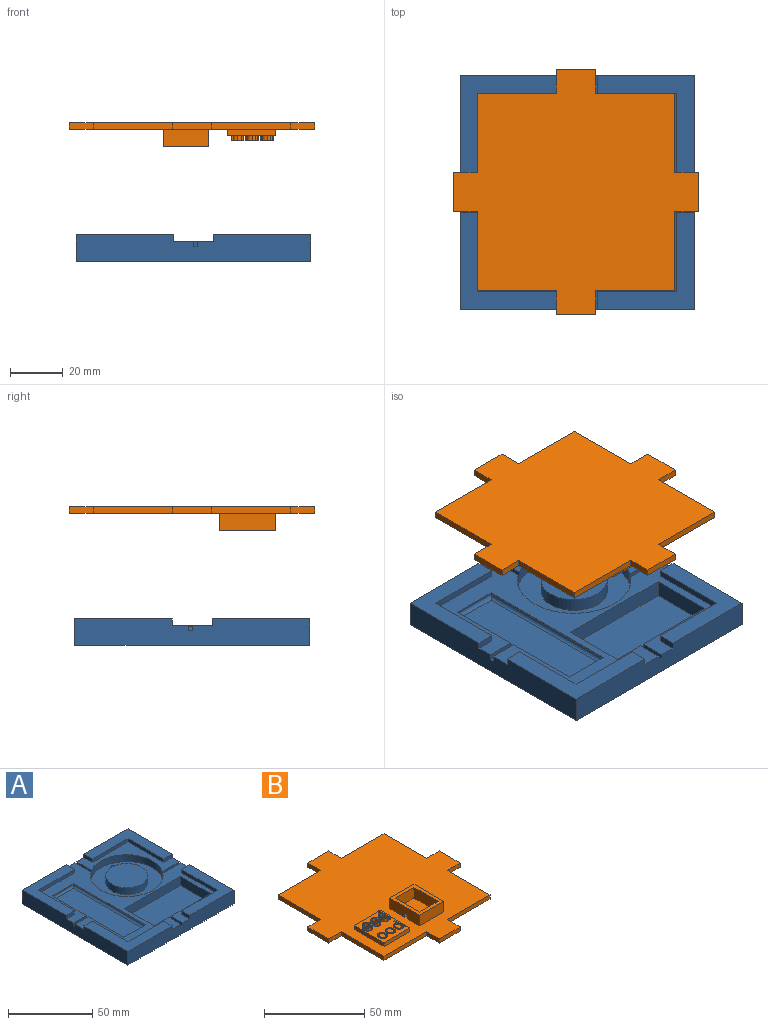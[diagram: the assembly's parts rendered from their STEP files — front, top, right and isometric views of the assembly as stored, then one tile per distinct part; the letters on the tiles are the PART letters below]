
ASSEMBLY  parts=2 mates=1
PART A: 59 faces, bbox 88.9x88.9x10 mm
  f0: cylinder r=21.5mm len=43mm, axis (0,0,1), area 662.5mm2, adj f1,f2,f40,f50,f51,f52,f53,f54
  f1: plane 42.95x42.95mm, normal (0,0,1), area 414.7mm2, adj f0,f3,f5,f14,f27,f28,f29,f50
  f2: plane 88.9x88.9mm, normal (0,0,1), area 1847.3mm2, adj f0,f3,f4,f5,f6,f7,f15,f16
  f3: plane 88.9x10mm, normal (1,0,0), area 844mm2, adj f1,f2,f4,f5,f9,f12,f13,f26
  f4: plane 88.9x10mm, normal (0,-1,0), area 848.5mm2, adj f2,f3,f6,f11,f12,f13,f22,f23
  f5: plane 88.9x10mm, normal (0,1,0), area 848.5mm2, adj f1,f2,f3,f6,f9,f10,f13,f14
  f6: plane 88.9x10mm, normal (-1,0,0), area 848.5mm2, adj f2,f4,f5,f10,f11,f13,f18,f19
  f7: plane 30x0.55mm, normal (1,0,0), area 16.5mm2, adj f2,f8,f33,f55
  f8: cylinder r=1.45mm len=30mm, axis (0,-1,0), area 67.1mm2, adj f7,f34,f37,f55
  f9: plane 36.95x36.95mm, normal (0,0,1), area 465.3mm2, adj f3,f5,f14,f27,f28,f29
  f10: plane 36.95x36.95mm, normal (0,0,1), area 465.3mm2, adj f5,f6,f15,f16,f17,f18
  f11: plane 36.95x36.95mm, normal (0,0,1), area 465.3mm2, adj f4,f6,f19,f20,f21,f22
  f12: plane 36.95x36.95mm, normal (0,0,1), area 465.3mm2, adj f3,f4,f23,f24,f25,f26
  f13: plane 88.9x88.9mm, normal (0,0,-1), area 7903.2mm2, adj f3,f4,f5,f6
  f14: plane 6.95x2.5mm, normal (-1,0,0), area 17.4mm2, adj f1,f5,f9,f29
  f15: plane 6.95x2.5mm, normal (1,0,0), area 17.4mm2, adj f2,f5,f10,f16
  f16: plane 30x2.5mm, normal (0,-1,0), area 75mm2, adj f2,f10,f15,f17
  f17: plane 30x2.5mm, normal (1,0,0), area 75mm2, adj f2,f10,f16,f18
  f18: plane 6.95x2.5mm, normal (0,-1,0), area 17.4mm2, adj f2,f6,f10,f17
  f19: plane 6.95x2.5mm, normal (0,1,0), area 17.4mm2, adj f2,f6,f11,f20
  f20: plane 30x2.5mm, normal (1,0,0), area 75mm2, adj f2,f11,f19,f21
  f21: plane 30x2.5mm, normal (0,1,0), area 75mm2, adj f2,f11,f20,f22
  f22: plane 6.95x2.5mm, normal (1,0,0), area 17.4mm2, adj f2,f4,f11,f21
  f23: plane 6.95x2.5mm, normal (-1,0,0), area 17.4mm2, adj f2,f4,f12,f24
  f24: plane 30x2.5mm, normal (0,1,0), area 75mm2, adj f2,f12,f23,f25
  f25: plane 30x2.5mm, normal (-1,0,0), area 75mm2, adj f2,f12,f24,f26
  f26: plane 6.95x2.5mm, normal (0,1,0), area 17.4mm2, adj f2,f3,f12,f25
  f27: plane 6.95x2.5mm, normal (0,-1,0), area 17.4mm2, adj f1,f3,f9,f28
  f28: plane 30x2.5mm, normal (-1,0,0), area 75mm2, adj f1,f9,f27,f29
  f29: plane 30x2.5mm, normal (0,-1,0), area 75mm2, adj f1,f9,f14,f28
  f30: plane 60x0.55mm, normal (-1,0,0), area 33.1mm2, adj f2,f31,f33,f35
  f31: plane 18x0.55mm, normal (0,-1,0), area 9.9mm2, adj f2,f30,f32,f36
  f32: plane 28.5x0.55mm, normal (1,0,0), area 15.7mm2, adj f2,f31,f38,f56
  f33: plane 18x0.55mm, normal (0,1,0), area 9.9mm2, adj f2,f7,f30,f37
  f34: plane 57.1x27.5mm, normal (0,0,1), area 881mm2, adj f6,f8,f35,f36,f37,f38,f55,f56
  f35: cylinder r=1.45mm len=60mm, axis (0,1,0), area 134.1mm2, adj f30,f34,f36,f37
  f36: cylinder r=1.45mm len=18mm, axis (-1,0,0), area 38.6mm2, adj f31,f34,f35,f38
  f37: cylinder r=1.45mm len=18mm, axis (1,0,0), area 38.6mm2, adj f8,f33,f34,f35
  f38: cylinder r=1.45mm len=28.5mm, axis (0,-1,0), area 63.6mm2, adj f32,f34,f36,f56
  f39: cylinder r=12.5mm len=25mm, axis (0,0,1), area 392.7mm2, adj f40,f41
  f40: plane 53.45x43mm, normal (0,0,1), area 975.5mm2, adj f0,f3,f39,f50,f51,f58
  f41: plane 25x25mm, normal (0,0,1), area 490.9mm2, adj f39
  f42: plane 47x6.5mm, normal (0,-1,0), area 305.5mm2, adj f2,f43,f45,f46
  f43: plane 25x6.5mm, normal (1,0,0), area 162.5mm2, adj f2,f42,f44,f46
  f44: plane 47x6.5mm, normal (0,1,0), area 302.5mm2, adj f2,f43,f45,f46,f47,f48,f49
  f45: plane 25x6.5mm, normal (-1,0,0), area 162.5mm2, adj f2,f42,f44,f46
  f46: plane 47x25mm, normal (0,0,1), area 1175mm2, adj f42,f43,f44,f45
  f47: plane 9.95x1.5mm, normal (0,0,1), area 14.9mm2, adj f4,f44,f48,f49
  f48: plane 9.95x2mm, normal (1,0,0), area 19.9mm2, adj f2,f4,f44,f47
  f49: plane 9.95x2mm, normal (-1,0,0), area 19.9mm2, adj f2,f4,f44,f47
  f50: plane 14.11x5mm, normal (0,-1,0), area 70.6mm2, adj f0,f1,f3,f40
  f51: plane 15.22x5mm, normal (0,1,0), area 76.1mm2, adj f0,f2,f3,f40
  f52: plane 13.46x1.5mm, normal (0,0,1), area 19.4mm2, adj f0,f5,f53,f54
  f53: plane 12.48x2mm, normal (-1,0,0), area 25mm2, adj f0,f1,f5,f52
  f54: plane 13.46x2mm, normal (1,0,0), area 26.9mm2, adj f0,f2,f5,f52
  f55: plane 12.4x2mm, normal (0,1,0), area 22.4mm2, adj f2,f6,f7,f8,f34
  f56: plane 12.4x2mm, normal (0,-1,0), area 22.4mm2, adj f2,f6,f32,f34,f38
  f57: plane 0.16x0.16mm, normal (0,0,1), area 0mm2, adj f58
  f58: torus R=0.08mm, axis (0,0,1), area 15.3mm2, adj f40,f57
PART B: 167 faces, bbox 92.8x92.8x9 mm
  f0: plane 21x18.16mm, normal (0,0,1), area 257.9mm2, adj f35,f36,f37,f38,f39,f40,f41,f42
  f1: plane 92.8x92.8mm, normal (0,0,1), area 5614.5mm2, adj f2,f3,f4,f5,f6,f7,f8,f9
  f2: plane 9x2.5mm, normal (-1,0,0), area 22.5mm2, adj f1,f3,f21,f22
  f3: plane 30x2.5mm, normal (0,1,0), area 75mm2, adj f1,f2,f4,f22
  f4: plane 30x2.5mm, normal (-1,0,0), area 75mm2, adj f1,f3,f5,f22
  f5: plane 9x2.5mm, normal (0,1,0), area 22.5mm2, adj f1,f4,f6,f22
  f6: plane 14.8x2.5mm, normal (-1,0,0), area 37mm2, adj f1,f5,f7,f22
  f7: plane 9x2.5mm, normal (0,-1,0), area 22.5mm2, adj f1,f6,f8,f22
  f8: plane 30x2.5mm, normal (-1,0,0), area 75mm2, adj f1,f7,f9,f22
  f9: plane 30x2.5mm, normal (0,-1,0), area 75mm2, adj f1,f8,f10,f22
  f10: plane 9x2.5mm, normal (-1,0,0), area 22.5mm2, adj f1,f9,f11,f22
  f11: plane 14.8x2.5mm, normal (0,-1,0), area 37mm2, adj f1,f10,f12,f22
  f12: plane 9x2.5mm, normal (1,0,0), area 22.5mm2, adj f1,f11,f13,f22
  f13: plane 30x2.5mm, normal (0,-1,0), area 75mm2, adj f1,f12,f14,f22
  f14: plane 30x2.5mm, normal (1,0,0), area 75mm2, adj f1,f13,f15,f22
  f15: plane 9x2.5mm, normal (0,-1,0), area 22.5mm2, adj f1,f14,f16,f22
  f16: plane 14.8x2.5mm, normal (1,0,0), area 37mm2, adj f1,f15,f17,f22
  f17: plane 9x2.5mm, normal (0,1,0), area 22.5mm2, adj f1,f16,f18,f22
  f18: plane 30x2.5mm, normal (1,0,0), area 75mm2, adj f1,f17,f19,f22
  f19: plane 30x2.5mm, normal (0,1,0), area 75mm2, adj f1,f18,f20,f22
  f20: plane 9x2.5mm, normal (1,0,0), area 22.5mm2, adj f1,f19,f21,f22
  f21: plane 14.8x2.5mm, normal (0,1,0), area 37mm2, adj f1,f2,f20,f22
  f22: plane 92.8x92.8mm, normal (0,0,-1), area 6127.8mm2, adj f2,f3,f4,f5,f6,f7,f8,f9
  f23: plane 17x6.48mm, normal (0,1,0), area 110.2mm2, adj f1,f24,f30,f31
  f24: plane 21x6.48mm, normal (-1,0,0), area 132.1mm2, adj f1,f23,f25,f31,f32,f33,f34
  f25: plane 17x6.48mm, normal (0,-1,0), area 110.2mm2, adj f1,f24,f30,f31
  f26: plane 13x6.48mm, normal (0,-1,0), area 84.2mm2, adj f1,f27,f29,f31
  f27: plane 17x6.48mm, normal (-1,0,0), area 110.2mm2, adj f1,f26,f28,f31
  f28: plane 13x6.48mm, normal (0,1,0), area 84.2mm2, adj f1,f27,f29,f31
  f29: plane 17x6.48mm, normal (1,0,0), area 106.2mm2, adj f1,f26,f28,f31,f32,f33,f34
  f30: plane 21x6.48mm, normal (1,0,0), area 136.1mm2, adj f1,f23,f25,f31
  f31: plane 21x17mm, normal (0,0,1), area 136mm2, adj f23,f24,f25,f26,f27,f28,f29,f30
  f32: plane 2x2mm, normal (0,-1,0), area 4mm2, adj f1,f24,f29,f34
  f33: plane 2x2mm, normal (0,1,0), area 4mm2, adj f1,f24,f29,f34
  f34: plane 2x2mm, normal (0,0,-1), area 4mm2, adj f24,f29,f32,f33
  f35: plane 18.16x2.3mm, normal (0,1,0), area 41.8mm2, adj f0,f1,f36,f38
  f36: plane 21x2.3mm, normal (-1,0,0), area 48.3mm2, adj f0,f1,f35,f37
  f37: plane 18.16x2.3mm, normal (0,-1,0), area 41.8mm2, adj f0,f1,f36,f38
  f38: plane 21x2.3mm, normal (1,0,0), area 48.3mm2, adj f0,f1,f35,f37
  f39: extruded ~1.93x1.9mm, area 3.9mm2, adj f0,f40,f47,f72
  f40: extruded ~1.91x1.9mm, area 3.9mm2, adj f0,f39,f41,f72
  f41: extruded ~1.9x1.68mm, area 3.6mm2, adj f0,f40,f42,f72
  f42: extruded ~1.9x1.72mm, area 3.6mm2, adj f0,f41,f43,f72
  f43: extruded ~1.93x1.9mm, area 3.9mm2, adj f0,f42,f44,f72
  f44: extruded ~1.9x1.39mm, area 2.7mm2, adj f0,f43,f45,f72
  f45: extruded ~1.9x0.91mm, area 2.4mm2, adj f0,f44,f46,f72
  f46: extruded ~1.9x1.2mm, area 2.4mm2, adj f0,f45,f47,f72
  f47: extruded ~1.9x1.72mm, area 3.6mm2, adj f0,f39,f46,f72
  f48: extruded ~1.93x1.9mm, area 3.9mm2, adj f0,f49,f56,f82
  f49: extruded ~1.91x1.9mm, area 3.9mm2, adj f0,f48,f50,f82
  f50: extruded ~1.9x1.68mm, area 3.6mm2, adj f0,f49,f51,f82
  f51: extruded ~1.9x1.72mm, area 3.6mm2, adj f0,f50,f52,f82
  f52: extruded ~1.93x1.9mm, area 3.9mm2, adj f0,f51,f53,f82
  f53: extruded ~1.9x1.39mm, area 2.7mm2, adj f0,f52,f54,f82
  f54: extruded ~1.9x0.91mm, area 2.4mm2, adj f0,f53,f55,f82
  f55: extruded ~1.9x1.2mm, area 2.4mm2, adj f0,f54,f56,f82
  f56: extruded ~1.9x1.72mm, area 3.6mm2, adj f0,f48,f55,f82
  f57: plane 1.9x0.04mm, normal (0,-1,0), area 0.1mm2, adj f0,f58,f71,f92
  f58: plane 1.9x0.68mm, normal (-0.99,-0.15,0), area 1.3mm2, adj f0,f57,f59,f92
  f59: plane 1.9x0.62mm, normal (0,-1,0), area 1.2mm2, adj f0,f58,f60,f92
  f60: plane 7.18x1.9mm, normal (1,0,0), area 13.6mm2, adj f0,f59,f61,f92
  f61: plane 1.9x0.77mm, normal (0,1,0), area 1.5mm2, adj f0,f60,f62,f92
  f62: plane 2.06x1.9mm, normal (-1,0,0), area 3.9mm2, adj f0,f61,f63,f92
  f63: plane 1.9x0.36mm, normal (-1,-0.05,0), area 0.7mm2, adj f0,f62,f64,f92
  f64: plane 1.9x0.36mm, normal (-1,-0.09,0), area 0.7mm2, adj f0,f63,f65,f92
  f65: plane 1.9x0.06mm, normal (0,1,0), area 0.1mm2, adj f0,f64,f66,f92
  f66: extruded ~1.9x1.58mm, area 3.5mm2, adj f0,f65,f67,f92
  f67: extruded ~1.9x1.54mm, area 3.3mm2, adj f0,f66,f68,f92
  f68: extruded ~1.94x1.9mm, area 3.9mm2, adj f0,f67,f69,f92
  f69: extruded ~1.93x1.9mm, area 3.9mm2, adj f0,f68,f70,f92
  f70: extruded ~1.9x1.54mm, area 3.3mm2, adj f0,f69,f71,f92
  f71: extruded ~1.9x1.59mm, area 3.5mm2, adj f0,f57,f70,f92
  f72: plane 5.24x4.64mm, normal (0,0,1), area 9.8mm2, adj f39,f40,f41,f42,f43,f44,f45,f46
  f73: plane 3.95x3.06mm, normal (0,0,1), area 10mm2, adj f74,f75,f76,f77,f78,f79,f80,f81
  f74: extruded ~1.9x1.14mm, area 2.5mm2, adj f72,f73,f75,f81
  f75: extruded ~1.9x1.14mm, area 2.5mm2, adj f72,f73,f74,f76
  f76: extruded ~1.9x1.48mm, area 3mm2, adj f72,f73,f75,f77
  f77: extruded ~1.9x1.46mm, area 2.9mm2, adj f72,f73,f76,f78
  f78: extruded ~1.9x1.15mm, area 2.5mm2, adj f72,f73,f77,f79
  f79: extruded ~1.9x1.13mm, area 2.4mm2, adj f72,f73,f78,f80
  f80: extruded ~1.9x1.47mm, area 2.9mm2, adj f72,f73,f79,f81
  f81: extruded ~1.9x1.48mm, area 3mm2, adj f72,f73,f74,f80
  f82: plane 5.24x4.64mm, normal (0,0,1), area 9.8mm2, adj f48,f49,f50,f51,f52,f53,f54,f55
  f83: plane 3.95x3.06mm, normal (0,0,1), area 10mm2, adj f84,f85,f86,f87,f88,f89,f90,f91
  f84: extruded ~1.9x1.14mm, area 2.5mm2, adj f82,f83,f85,f91
  f85: extruded ~1.9x1.14mm, area 2.5mm2, adj f82,f83,f84,f86
  f86: extruded ~1.9x1.48mm, area 3mm2, adj f82,f83,f85,f87
  f87: extruded ~1.9x1.46mm, area 2.9mm2, adj f82,f83,f86,f88
  f88: extruded ~1.9x1.15mm, area 2.5mm2, adj f82,f83,f87,f89
  f89: extruded ~1.9x1.13mm, area 2.4mm2, adj f82,f83,f88,f90
  f90: extruded ~1.9x1.47mm, area 2.9mm2, adj f82,f83,f89,f91
  f91: extruded ~1.9x1.48mm, area 3mm2, adj f82,f83,f84,f90
  f92: plane 7.27x4.45mm, normal (0,0,1), area 12.5mm2, adj f57,f58,f59,f60,f61,f62,f63,f64
  f93: plane 3.96x2.89mm, normal (0,0,1), area 9.6mm2, adj f94,f95,f96,f97,f98,f99,f100,f101
  f94: extruded ~1.9x1.38mm, area 2.8mm2, adj f92,f93,f95,f102
  f95: plane 1.9x0.16mm, normal (-1,0,0), area 0.3mm2, adj f92,f93,f94,f96
  f96: extruded ~1.9x1.53mm, area 3mm2, adj f92,f93,f95,f97
  f97: extruded ~1.9x1.14mm, area 2.4mm2, adj f92,f93,f96,f98
  f98: extruded ~1.9x1.03mm, area 2.3mm2, adj f92,f93,f97,f99
  f99: extruded ~1.9x1.48mm, area 2.9mm2, adj f92,f93,f98,f100
  f100: extruded ~1.9x1.46mm, area 2.9mm2, adj f92,f93,f99,f101
  f101: extruded ~1.9x1.04mm, area 2.3mm2, adj f92,f93,f100,f102
  f102: extruded ~1.9x1.14mm, area 2.4mm2, adj f92,f93,f94,f101
  f103: extruded ~1.14x1mm, area 1.3mm2, adj f104,f126,f127,f164
  f104: extruded ~1.04x1mm, area 1.2mm2, adj f103,f105,f127,f164
  f105: extruded ~1.46x1mm, area 1.5mm2, adj f104,f106,f127,f164
  f106: extruded ~1.48x1mm, area 1.5mm2, adj f105,f107,f127,f164
  f107: extruded ~1.03x1mm, area 1.2mm2, adj f106,f108,f127,f164
  f108: extruded ~1.14x1mm, area 1.3mm2, adj f107,f109,f127,f164
  f109: extruded ~1.53x1mm, area 1.6mm2, adj f108,f110,f127,f164
  f110: plane 1x0.16mm, normal (1,0,0), area 0.2mm2, adj f109,f126,f127,f164
  f111: plane 1x0.04mm, normal (0,1,0), area 0mm2, adj f0,f112,f125,f127
  f112: plane 1x0.68mm, normal (0.99,0.15,0), area 0.7mm2, adj f0,f111,f113,f127
  f113: plane 1x0.62mm, normal (0,1,0), area 0.6mm2, adj f0,f112,f114,f127
  f114: plane 7.18x1mm, normal (-1,0,0), area 7.2mm2, adj f0,f113,f115,f127
  f115: plane 1x0.77mm, normal (0,-1,0), area 0.8mm2, adj f0,f114,f116,f127
  f116: plane 2.06x1mm, normal (1,0,0), area 2.1mm2, adj f0,f115,f117,f127
  f117: plane 1x0.36mm, normal (1,0.05,0), area 0.4mm2, adj f0,f116,f118,f127
  f118: plane 1x0.36mm, normal (1,0.09,0), area 0.4mm2, adj f0,f117,f119,f127
  f119: plane 1x0.06mm, normal (0,-1,0), area 0.1mm2, adj f0,f118,f120,f127
  f120: extruded ~1.58x1mm, area 1.8mm2, adj f0,f119,f121,f127
  f121: extruded ~1.54x1mm, area 1.8mm2, adj f0,f120,f122,f127
  f122: extruded ~1.94x1mm, area 2.1mm2, adj f0,f121,f123,f127
  f123: extruded ~1.93x1mm, area 2mm2, adj f0,f122,f124,f127
  f124: extruded ~1.54x1mm, area 1.7mm2, adj f0,f123,f125,f127
  f125: extruded ~1.59x1mm, area 1.8mm2, adj f0,f111,f124,f127
  f126: extruded ~1.38x1mm, area 1.4mm2, adj f103,f110,f127,f164
  f127: plane 7.27x4.45mm, normal (0,0,1), area 12.5mm2, adj f103,f104,f105,f106,f107,f108,f109,f110
  f128: extruded ~1.48x1mm, area 1.6mm2, adj f129,f144,f145,f165
  f129: extruded ~1.47x1mm, area 1.5mm2, adj f128,f130,f145,f165
  f130: extruded ~1.13x1mm, area 1.3mm2, adj f129,f131,f145,f165
  f131: extruded ~1.15x1mm, area 1.3mm2, adj f130,f132,f145,f165
  f132: extruded ~1.46x1mm, area 1.5mm2, adj f131,f133,f145,f165
  f133: extruded ~1.48x1mm, area 1.6mm2, adj f132,f134,f145,f165
  f134: extruded ~1.14x1mm, area 1.3mm2, adj f133,f144,f145,f165
  f135: extruded ~1.93x1mm, area 2.1mm2, adj f0,f136,f143,f145
  f136: extruded ~1.91x1mm, area 2.1mm2, adj f0,f135,f137,f145
  f137: extruded ~1.68x1mm, area 1.9mm2, adj f0,f136,f138,f145
  f138: extruded ~1.72x1mm, area 1.9mm2, adj f0,f137,f139,f145
  f139: extruded ~1.93x1mm, area 2.1mm2, adj f0,f138,f140,f145
  f140: extruded ~1.39x1mm, area 1.4mm2, adj f0,f139,f141,f145
  f141: extruded ~1x0.91mm, area 1.2mm2, adj f0,f140,f142,f145
  f142: extruded ~1.2x1mm, area 1.3mm2, adj f0,f141,f143,f145
  f143: extruded ~1.72x1mm, area 1.9mm2, adj f0,f135,f142,f145
  f144: extruded ~1.14x1mm, area 1.3mm2, adj f128,f134,f145,f165
  f145: plane 5.24x4.64mm, normal (0,0,1), area 9.8mm2, adj f128,f129,f130,f131,f132,f133,f134,f135
  f146: extruded ~1.48x1mm, area 1.6mm2, adj f147,f162,f163,f166
  f147: extruded ~1.47x1mm, area 1.5mm2, adj f146,f148,f163,f166
  f148: extruded ~1.13x1mm, area 1.3mm2, adj f147,f149,f163,f166
  f149: extruded ~1.15x1mm, area 1.3mm2, adj f148,f150,f163,f166
  f150: extruded ~1.46x1mm, area 1.5mm2, adj f149,f151,f163,f166
  f151: extruded ~1.48x1mm, area 1.6mm2, adj f150,f152,f163,f166
  f152: extruded ~1.14x1mm, area 1.3mm2, adj f151,f162,f163,f166
  f153: extruded ~1.93x1mm, area 2.1mm2, adj f0,f154,f161,f163
  f154: extruded ~1.91x1mm, area 2.1mm2, adj f0,f153,f155,f163
  f155: extruded ~1.68x1mm, area 1.9mm2, adj f0,f154,f156,f163
  f156: extruded ~1.72x1mm, area 1.9mm2, adj f0,f155,f157,f163
  f157: extruded ~1.93x1mm, area 2.1mm2, adj f0,f156,f158,f163
  f158: extruded ~1.39x1mm, area 1.4mm2, adj f0,f157,f159,f163
  f159: extruded ~1x0.91mm, area 1.2mm2, adj f0,f158,f160,f163
  f160: extruded ~1.2x1mm, area 1.3mm2, adj f0,f159,f161,f163
  f161: extruded ~1.72x1mm, area 1.9mm2, adj f0,f153,f160,f163
  f162: extruded ~1.14x1mm, area 1.3mm2, adj f146,f152,f163,f166
  f163: plane 5.24x4.64mm, normal (0,0,1), area 9.8mm2, adj f146,f147,f148,f149,f150,f151,f152,f153
  f164: plane 3.96x2.89mm, normal (0,0,1), area 9.6mm2, adj f103,f104,f105,f106,f107,f108,f109,f110
  f165: plane 3.95x3.06mm, normal (0,0,1), area 10mm2, adj f128,f129,f130,f131,f132,f133,f134,f144
  f166: plane 3.95x3.06mm, normal (0,0,1), area 10mm2, adj f146,f147,f148,f149,f150,f151,f152,f162
PLACE A rot(axis=(0,0,1),0deg) t=(57.39,-12.43,-8.38)mm
PLACE B rot(axis=(0,-1,0),180deg) t=(56.85,-12.35,44.12)mm
MATE slider B.f1 <-> A.f13  axis (0,0,-1) through (55.39,-10.43,41.62)mm
